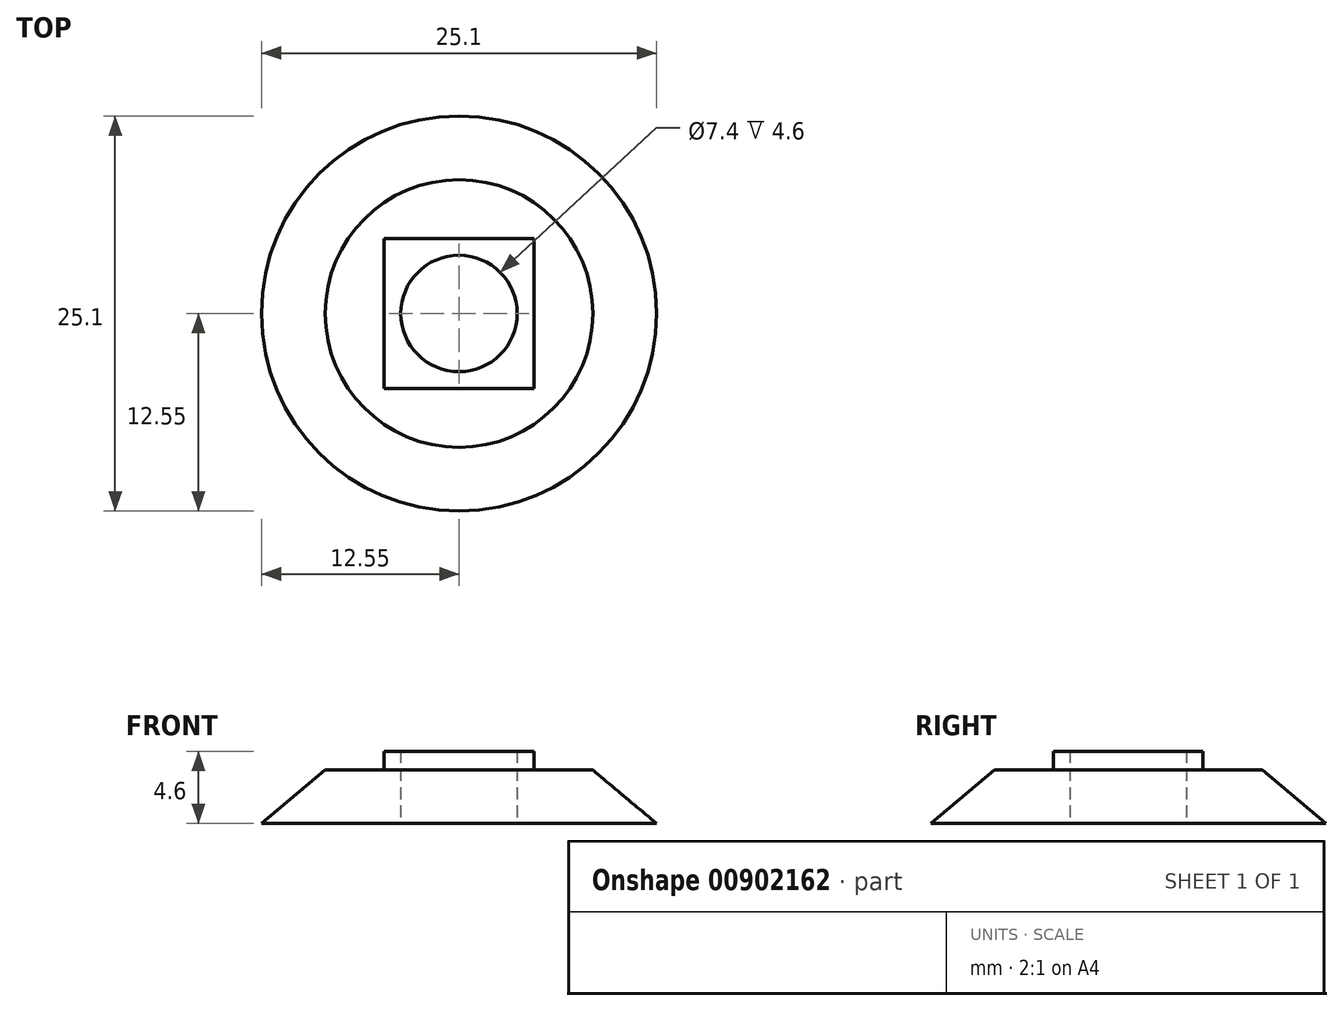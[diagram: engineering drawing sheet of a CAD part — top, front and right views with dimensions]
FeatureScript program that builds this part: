
annotation { "Feature Type Name" : "Feature", "Feature Type Description" : "" }
export const myFeature = defineFeature(function(context is Context, id is Id, definition is map)
    precondition{}
    {
        {
            var Q0;
            Q0=qCreatedBy(makeId("Top.planeOp"),FACE);
            var sketch = newSketch(context, id + "F0", { "sketchPlane" : qUnion([Q0])});
            skCircle(sketch, "E0", {"center": v(0, 0) * mm, "radius": 14 * mm});
            skCircle(sketch, "E1", {"center": v(0, 0) * mm, "radius": 3.7 * mm});
            skLineSegment(sketch, "E2.bottom", {"start": v(4.75, -4.75) * mm, "end": v(-4.75, -4.75) * mm});
            skLineSegment(sketch, "E2.top", {"start": v(4.75, 4.75) * mm, "end": v(-4.75, 4.75) * mm});
            skLineSegment(sketch, "E2.left", {"start": v(4.75, -4.75) * mm, "end": v(4.75, 4.75) * mm});
            skLineSegment(sketch, "E2.right", {"start": v(-4.75, -4.75) * mm, "end": v(-4.75, 4.75) * mm});
            skSolve(sketch);
        }
        {
            var Q0;
            Q0=makeQuery(id+"F0.imprint","IMPRINT",FACE,{"disambiguationData":[TD([[makeQuery(id+"F0.imprint","IMPRINT",EDGE,{"derivedFrom":sQuery(id+"F0.wireOp",EDGE,"E0")}),1.0]])]});
            extrude(context, id + "F1", {"entities" : qUnion([Q0]), "depth" : 3.4 * mm, "offsetDistance" : 25 * mm});
        }
        {
            var Q0;
            Q0=makeQuery(id+"F0.imprint","IMPRINT",FACE,{"disambiguationData":[TD([[makeQuery(id+"F0.imprint","IMPRINT",EDGE,{"derivedFrom":sQuery(id+"F0.wireOp",EDGE,"E1")}),-1.0]])]});
            extrude(context, id + "F2", {"entities" : qUnion([Q0]), "operationType" : NewBodyOperationType.ADD, "depth" : 4.6 * mm, "offsetDistance" : 25 * mm});
        }
        {
            var Q0;
            Q0=makeQuery(id+"F1.opExtrude","CAP_EDGE",EDGE,{"disambiguationData":[OSD([sQuery(id+"F0.wireOp",EDGE,"E0")])],"isStart":false});
            chamfer(context, id + "F3", {"entities" : qUnion([Q0]), "chamferType" : ChamferType.OFFSET_ANGLE, "width" : 5.5 * mm, "oppositeDirection" : false, "angle" : 40 * degree, "tangentPropagation" : true});
        }
    });
